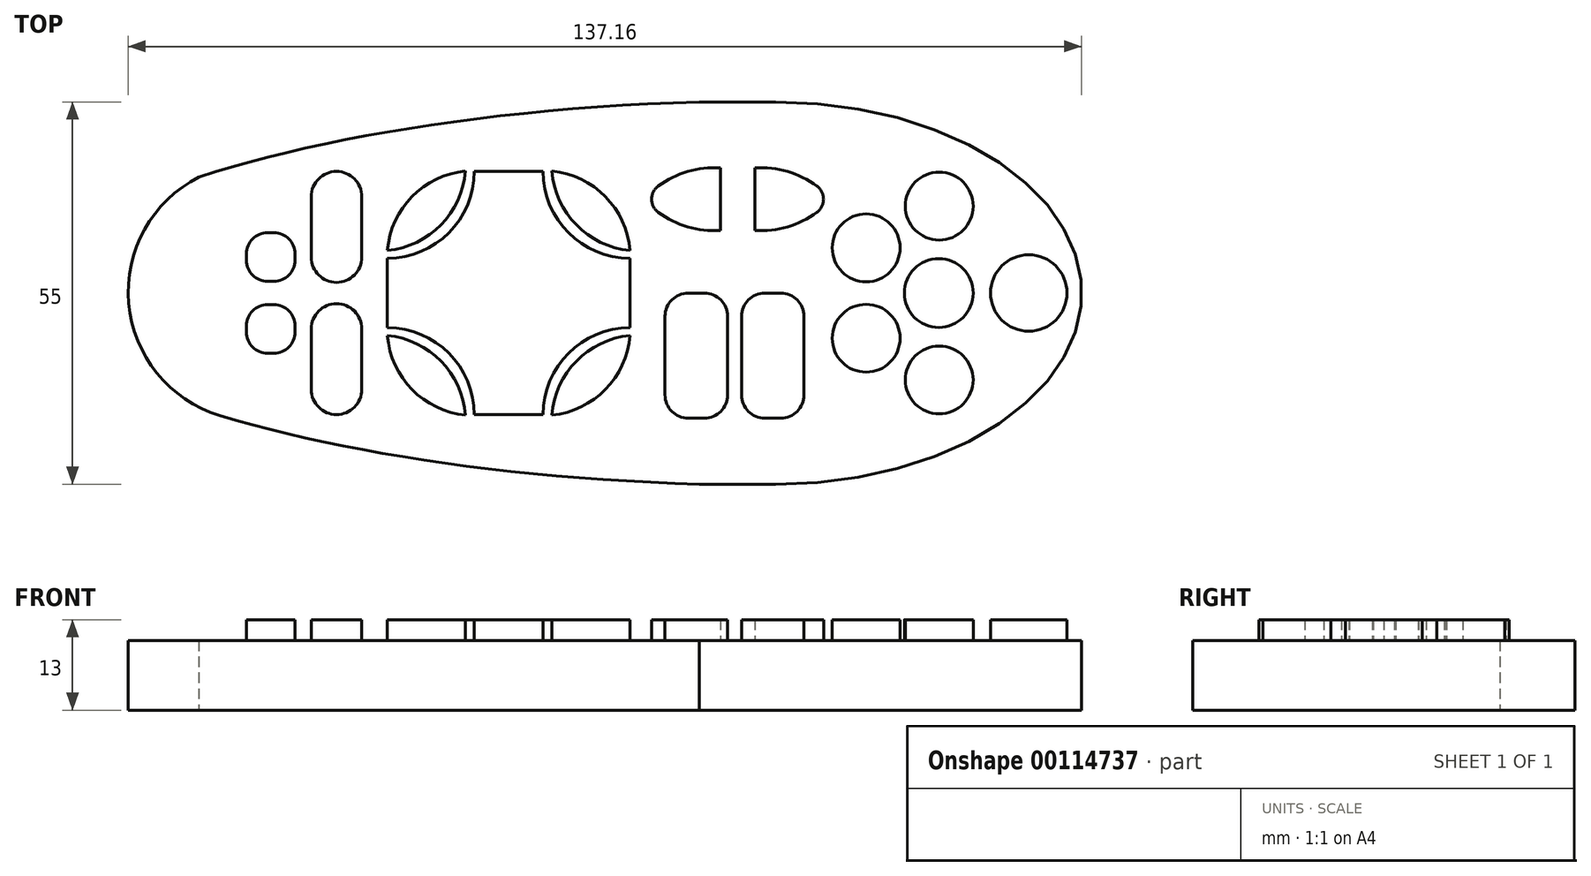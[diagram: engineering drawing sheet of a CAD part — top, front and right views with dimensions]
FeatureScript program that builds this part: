
annotation { "Feature Type Name" : "Feature", "Feature Type Description" : "" }
export const myFeature = defineFeature(function(context is Context, id is Id, definition is map)
    precondition{}
    {
        {
            var Q0;
            Q0=qCreatedBy(makeId("Top.planeOp"),FACE);
            var sketch = newSketch(context, id + "F0", { "sketchPlane" : qUnion([Q0])});
            skLineSegment(sketch, "E0.bottom", {"start": v(17, 27.5) * mm, "end": v(28, 27.5) * mm});
            skPoint(sketch, "E1", {"position": v(28, 27.5) * mm});
            skPoint(sketch, "E2", {"position": v(28, -27.5) * mm});
            skEllipticalArc(sketch, "E3", {});
            skPoint(sketch, "E4", {"position": v(17, 27.5) * mm});
            skPoint(sketch, "E5", {"position": v(17, -27.5) * mm});
            skPoint(sketch, "E6.startSnap0", {"position": v(71.98, 0) * mm});
            skLineSegment(sketch, "E7", {"start": v(17, -27.5) * mm, "end": v(28, -27.5) * mm});
            skEllipticalArc(sketch, "E8.MirrorCS", {});
            skFitSpline(sketch, "E9", {"points": [v(17, 27.5) * mm, v(-78.58, 0) * mm, v(17, -27.5) * mm, v(157.43, 0) * mm, v(17, 27.5) * mm]});
            skPoint(sketch, "E10.MirrorCS.start.orphan", {"position": v(17.03, 27.5) * mm});
            skPoint(sketch, "E11.MirrorCS.start.orphan", {"position": v(17.03, -27.5) * mm});
            skLineSegment(sketch, "E12", {"start": v(-55, 16.67) * mm, "end": v(-55, 16.67) * mm});
            skArc(sketch, "E13", {"start": v(-52.03, -17.6) * mm, "mid": v(-65.1, -1.47) * mm, "end": v(-55, 16.67) * mm});
            const initialGuessF0  = {"E3": [0.027990437101635235, 0, 1, 0, 0.04399372289882635, 0.0275, 0, 1.5707963267948966], "E8.MirrorCS": [0.027990437101635235, 0, 1, 0, 0.04399372289882635, 0.0275, 4.71238898038469, 0]};
            skSetInitialGuess(sketch, initialGuessF0);
            skSolve(sketch);
        }
        {
            var Q0;
            Q0=makeQuery(id+"F0.imprint","IMPRINT",FACE,{"disambiguationData":[TD([[makeQuery(id+"F0.imprint","IMPRINT",EDGE,{"derivedFrom":sQuery(id+"F0.wireOp",EDGE,"E7")}),1.0]])]});
            var Q1;
            Q1=makeQuery(id+"F0.imprint","IMPRINT",FACE,{"disambiguationData":[TD([[makeQuery(id+"F0.imprint","IMPRINT",EDGE,{"derivedFrom":sQuery(id+"F0.wireOp",EDGE,"E0.bottom")}),-1.0]])]});
            extrude(context, id + "F1", {"entities" : qUnion([Q0, Q1]), "depth" : 10 * mm});
        }
        {
            var Q0;
            Q0=makeQuery(id+"F1.opExtrude","CAP_FACE",FACE,{"disambiguationData":[OSD([sQuery(id+"F0.wireOp",EDGE,"E0.bottom"),sQuery(id+"F0.wireOp",EDGE,"E3"),sQuery(id+"F0.wireOp",EDGE,"E7"),sQuery(id+"F0.wireOp",EDGE,"E8.MirrorCS"),sQuery(id+"F0.wireOp",EDGE,"E9"),sQuery(id+"F0.wireOp",EDGE,"E9"),sQuery(id+"F0.wireOp",EDGE,"E13")])],"isStart":false});
            var sketch = newSketch(context, id + "F2", { "sketchPlane" : qUnion([Q0])});
            skCircle(sketch, "E14", {"center": v(64.38, 0) * mm, "radius": 5.5 * mm});
            skCircle(sketch, "E15", {"center": v(51.44, 0) * mm, "radius": 4.95 * mm});
            skPoint(sketch, "E16", {"position": v(56.38, 0) * mm});
            skCircle(sketch, "E17", {"center": v(51.5, 12.5) * mm, "radius": 4.88 * mm});
            skCircle(sketch, "E18", {"center": v(51.5, -12.5) * mm, "radius": 4.88 * mm});
            skPoint(sketch, "E19", {"position": v(41, 0) * mm});
            skCircle(sketch, "E20", {"center": v(41, 6.5) * mm, "radius": 4.88 * mm});
            skCircle(sketch, "E21", {"center": v(41, -6.5) * mm, "radius": 4.88 * mm});
            skLineSegment(sketch, "E22.bottom", {"start": v(28.7, 0) * mm, "end": v(26.4, 0) * mm});
            skLineSegment(sketch, "E22.top", {"start": v(28.7, -18) * mm, "end": v(26.4, -18) * mm});
            skLineSegment(sketch, "E22.left", {"start": v(32.05, -3.35) * mm, "end": v(32.05, -14.65) * mm});
            skLineSegment(sketch, "E22.right", {"start": v(23.05, -3.35) * mm, "end": v(23.05, -14.65) * mm});
            skArc(sketch, "E23.filletArc", {"start": v(32.05, -3.35) * mm, "mid": v(31.07, -0.98) * mm, "end": v(28.7, 0) * mm});
            skArc(sketch, "E24.filletArc", {"start": v(26.4, 0) * mm, "mid": v(24.03, -0.98) * mm, "end": v(23.05, -3.35) * mm});
            skArc(sketch, "E25.filletArc", {"start": v(23.05, -14.65) * mm, "mid": v(24.03, -17.02) * mm, "end": v(26.4, -18) * mm});
            skArc(sketch, "E26.filletArc", {"start": v(28.7, -18) * mm, "mid": v(31.07, -17.02) * mm, "end": v(32.05, -14.65) * mm});
            skLineSegment(sketch, "E27.bottom", {"start": v(17.7, 0) * mm, "end": v(15.4, 0) * mm});
            skLineSegment(sketch, "E27.top", {"start": v(17.7, -18) * mm, "end": v(15.4, -18) * mm});
            skLineSegment(sketch, "E27.left", {"start": v(21.05, -3.35) * mm, "end": v(21.05, -14.65) * mm});
            skLineSegment(sketch, "E27.right", {"start": v(12.05, -3.35) * mm, "end": v(12.05, -14.65) * mm});
            skArc(sketch, "E28.filletArc", {"start": v(21.05, -3.35) * mm, "mid": v(20.07, -0.98) * mm, "end": v(17.7, 0) * mm});
            skArc(sketch, "E29.filletArc", {"start": v(15.4, 0) * mm, "mid": v(13.03, -0.98) * mm, "end": v(12.05, -3.35) * mm});
            skArc(sketch, "E30.filletArc", {"start": v(12.05, -14.65) * mm, "mid": v(13.03, -17.02) * mm, "end": v(15.4, -18) * mm});
            skArc(sketch, "E31.filletArc", {"start": v(17.7, -18) * mm, "mid": v(20.07, -17.02) * mm, "end": v(21.05, -14.65) * mm});
            skLineSegment(sketch, "E32", {"start": v(25, 9) * mm, "end": v(20, 9) * mm});
            skArc(sketch, "E33", {"start": v(33.89, 15.41) * mm, "mid": v(29.67, 17.49) * mm, "end": v(25, 18) * mm});
            skArc(sketch, "E34.MirrorCS", {"start": v(33.89, 11.59) * mm, "mid": v(29.67, 9.51) * mm, "end": v(25, 9) * mm});
            skArc(sketch, "E35.filletArc", {"start": v(33.89, 11.59) * mm, "mid": v(34.86, 13.5) * mm, "end": v(33.89, 15.41) * mm});
            skLineSegment(sketch, "E36", {"start": v(25, 18) * mm, "end": v(25, 9) * mm});
            skArc(sketch, "E37.MirrorCS", {"start": v(11.1, 15.41) * mm, "mid": v(15.32, 17.49) * mm, "end": v(20, 18) * mm});
            skArc(sketch, "E38.MirrorCS", {"start": v(11.1, 11.59) * mm, "mid": v(15.32, 9.51) * mm, "end": v(20, 9) * mm});
            skArc(sketch, "E39.MirrorCS", {"start": v(11.1, 11.59) * mm, "mid": v(10.13, 13.5) * mm, "end": v(11.1, 15.41) * mm});
            skLineSegment(sketch, "E40.MirrorCS", {"start": v(20, 18) * mm, "end": v(20, 9) * mm});
            skLineSegment(sketch, "E41.bottom", {"start": v(-5.5, -17.5) * mm, "end": v(-15.39, -17.5) * mm});
            skLineSegment(sketch, "E41.top", {"start": v(-5.5, 17.5) * mm, "end": v(-15.39, 17.5) * mm});
            skLineSegment(sketch, "E41.left", {"start": v(7, -5) * mm, "end": v(7, 5) * mm});
            skLineSegment(sketch, "E41.right", {"start": v(-27.89, -5) * mm, "end": v(-27.89, 5) * mm});
            skArc(sketch, "E42", {"start": v(7, -5) * mm, "mid": v(-1.84, -8.66) * mm, "end": v(-5.5, -17.5) * mm});
            skLineSegment(sketch, "E43", {"start": v(-10.44, 17.5) * mm, "end": v(-10.44, -17.5) * mm});
            skArc(sketch, "E44.MirrorCS", {"start": v(-27.89, -5) * mm, "mid": v(-19.05, -8.66) * mm, "end": v(-15.39, -17.5) * mm});
            skArc(sketch, "E45.MirrorCS", {"start": v(7, 5) * mm, "mid": v(-1.84, 8.66) * mm, "end": v(-5.5, 17.5) * mm});
            skArc(sketch, "E46.MirrorCS", {"start": v(-27.89, 5) * mm, "mid": v(-19.05, 8.66) * mm, "end": v(-15.39, 17.5) * mm});
            skArc(sketch, "E47.MirrorCS", {"start": v(7, 6.11) * mm, "mid": v(-0.69, 9.8) * mm, "end": v(-4.23, 17.56) * mm});
            skLineSegment(sketch, "E48", {"start": v(7, 6.05) * mm, "end": v(7, 6.11) * mm});
            skArc(sketch, "E49.MirrorCS", {"start": v(7, 6.11) * mm, "mid": v(3.46, 13.87) * mm, "end": v(-4.23, 17.56) * mm});
            skArc(sketch, "E50.MirrorCS", {"start": v(7, -6.11) * mm, "mid": v(-0.69, -9.8) * mm, "end": v(-4.23, -17.56) * mm});
            skArc(sketch, "E51.MirrorCS", {"start": v(7, -6.11) * mm, "mid": v(3.46, -13.87) * mm, "end": v(-4.23, -17.56) * mm});
            skArc(sketch, "E52.MirrorCS", {"start": v(-27.89, 6.11) * mm, "mid": v(-20.2, 9.8) * mm, "end": v(-16.66, 17.56) * mm});
            skArc(sketch, "E53.MirrorCS", {"start": v(-27.89, 6.11) * mm, "mid": v(-24.35, 13.87) * mm, "end": v(-16.66, 17.56) * mm});
            skArc(sketch, "E54.MirrorCS", {"start": v(-27.89, -6.11) * mm, "mid": v(-20.2, -9.8) * mm, "end": v(-16.66, -17.56) * mm});
            skArc(sketch, "E55.MirrorCS", {"start": v(-27.89, -6.11) * mm, "mid": v(-24.35, -13.87) * mm, "end": v(-16.66, -17.56) * mm});
            skLineSegment(sketch, "E56.bottom", {"start": v(-35.21, 1.53) * mm, "end": v(-35.21, 1.53) * mm});
            skLineSegment(sketch, "E56.top", {"start": v(-35.21, 17.5) * mm, "end": v(-35.21, 17.5) * mm});
            skLineSegment(sketch, "E56.left", {"start": v(-38.85, 5.17) * mm, "end": v(-38.85, 13.85) * mm});
            skLineSegment(sketch, "E56.right", {"start": v(-31.58, 5.17) * mm, "end": v(-31.58, 13.85) * mm});
            skArc(sketch, "E57.filletArc", {"start": v(-35.21, 1.53) * mm, "mid": v(-32.64, 2.6) * mm, "end": v(-31.58, 5.17) * mm});
            skArc(sketch, "E58.filletArc", {"start": v(-38.85, 5.17) * mm, "mid": v(-37.79, 2.6) * mm, "end": v(-35.21, 1.53) * mm});
            skArc(sketch, "E59.filletArc", {"start": v(-31.58, 13.85) * mm, "mid": v(-32.64, 16.43) * mm, "end": v(-35.21, 17.5) * mm});
            skArc(sketch, "E60.filletArc", {"start": v(-35.21, 17.5) * mm, "mid": v(-37.79, 16.43) * mm, "end": v(-38.85, 13.85) * mm});
            skPoint(sketch, "E61", {"position": v(-35.21, 17.5) * mm});
            skPoint(sketch, "E62", {"position": v(-35.21, 1.53) * mm});
            skPoint(sketch, "E63.endSnap0", {"position": v(-65.1, -1.47) * mm});
            skLineSegment(sketch, "E64.MirrorCS", {"start": v(-31.58, -5.17) * mm, "end": v(-31.58, -13.85) * mm});
            skArc(sketch, "E65.MirrorCS", {"start": v(-35.21, -1.53) * mm, "mid": v(-32.64, -2.6) * mm, "end": v(-31.58, -5.17) * mm});
            skArc(sketch, "E66.MirrorCS", {"start": v(-38.85, -5.17) * mm, "mid": v(-37.79, -2.6) * mm, "end": v(-35.21, -1.53) * mm});
            skLineSegment(sketch, "E67.MirrorCS", {"start": v(-38.85, -5.17) * mm, "end": v(-38.85, -13.85) * mm});
            skArc(sketch, "E68.MirrorCS", {"start": v(-35.21, -17.5) * mm, "mid": v(-37.79, -16.43) * mm, "end": v(-38.85, -13.85) * mm});
            skArc(sketch, "E69.MirrorCS", {"start": v(-31.58, -13.85) * mm, "mid": v(-32.64, -16.43) * mm, "end": v(-35.21, -17.5) * mm});
            skLineSegment(sketch, "E70.bottom", {"start": v(-45.13, 1.67) * mm, "end": v(-44.23, 1.67) * mm});
            skLineSegment(sketch, "E70.top", {"start": v(-45.13, 8.67) * mm, "end": v(-44.23, 8.67) * mm});
            skLineSegment(sketch, "E70.left", {"start": v(-48.18, 4.72) * mm, "end": v(-48.18, 5.63) * mm});
            skLineSegment(sketch, "E70.right", {"start": v(-41.18, 4.72) * mm, "end": v(-41.18, 5.63) * mm});
            skPoint(sketch, "E70.middle", {"position": v(-44.68, 5.17) * mm});
            skArc(sketch, "E71.filletArc", {"start": v(-44.23, 1.67) * mm, "mid": v(-42.07, 2.57) * mm, "end": v(-41.18, 4.72) * mm});
            skArc(sketch, "E72.filletArc", {"start": v(-48.18, 4.72) * mm, "mid": v(-47.29, 2.57) * mm, "end": v(-45.13, 1.67) * mm});
            skArc(sketch, "E73.filletArc", {"start": v(-45.13, 8.67) * mm, "mid": v(-47.29, 7.78) * mm, "end": v(-48.18, 5.63) * mm});
            skArc(sketch, "E74.filletArc", {"start": v(-41.18, 5.63) * mm, "mid": v(-42.07, 7.78) * mm, "end": v(-44.23, 8.67) * mm});
            skArc(sketch, "E75.MirrorCS", {"start": v(-44.23, -1.67) * mm, "mid": v(-42.07, -2.57) * mm, "end": v(-41.18, -4.72) * mm});
            skLineSegment(sketch, "E76.MirrorCS", {"start": v(-45.13, -1.67) * mm, "end": v(-44.23, -1.67) * mm});
            skArc(sketch, "E77.MirrorCS", {"start": v(-48.18, -4.72) * mm, "mid": v(-47.29, -2.57) * mm, "end": v(-45.13, -1.67) * mm});
            skLineSegment(sketch, "E78.MirrorCS", {"start": v(-48.18, -4.72) * mm, "end": v(-48.18, -5.63) * mm});
            skArc(sketch, "E79.MirrorCS", {"start": v(-45.13, -8.67) * mm, "mid": v(-47.29, -7.78) * mm, "end": v(-48.18, -5.63) * mm});
            skLineSegment(sketch, "E80.MirrorCS", {"start": v(-45.13, -8.67) * mm, "end": v(-44.23, -8.67) * mm});
            skArc(sketch, "E81.MirrorCS", {"start": v(-41.18, -5.63) * mm, "mid": v(-42.07, -7.78) * mm, "end": v(-44.23, -8.67) * mm});
            skLineSegment(sketch, "E82.MirrorCS", {"start": v(-41.18, -4.72) * mm, "end": v(-41.18, -5.63) * mm});
            skSolve(sketch);
        }
        {
            var Q0;
            Q0 = qSketchRegion(id + "F2", true);
            extrude(context, id + "F3", {"entities" : qUnion([Q0]), "operationType" : NewBodyOperationType.ADD, "depth" : 3 * mm});
        }
    });
